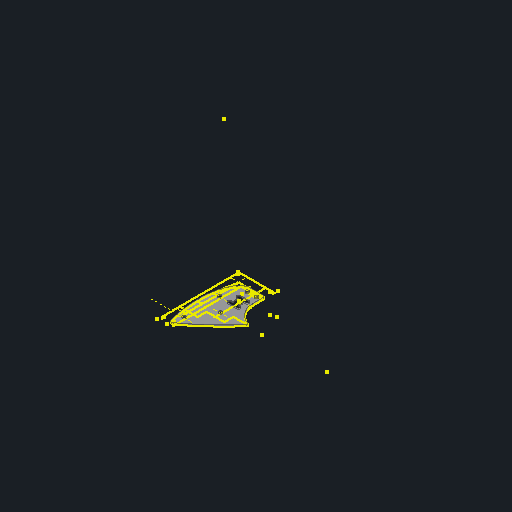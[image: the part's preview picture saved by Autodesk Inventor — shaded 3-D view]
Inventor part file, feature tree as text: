
AUTODESK INVENTOR PART (.ipt)
format: ipt  version: 2024 (Build 280153000, 153)  size: 173,568 bytes
history: native  units: in
note: dims shown in document units (in); Inventor stores cm internally (conversion verified against a paired STEP export)
features: other x3, sketch x1
ambient origin geometry x8: Origin, YZ Plane, XZ Plane, XY Plane, X Axis, Y Axis, Z Axis, Center Point
bodies: Solid1 (feature_tree)
feature tree (4):
  other  "sled2.ipt"
  other  "Solid1::sled2.ipt"
  other  "TaggingFeature1"
  sketch  "Sketch3"  dims[d0=0.3937in]
